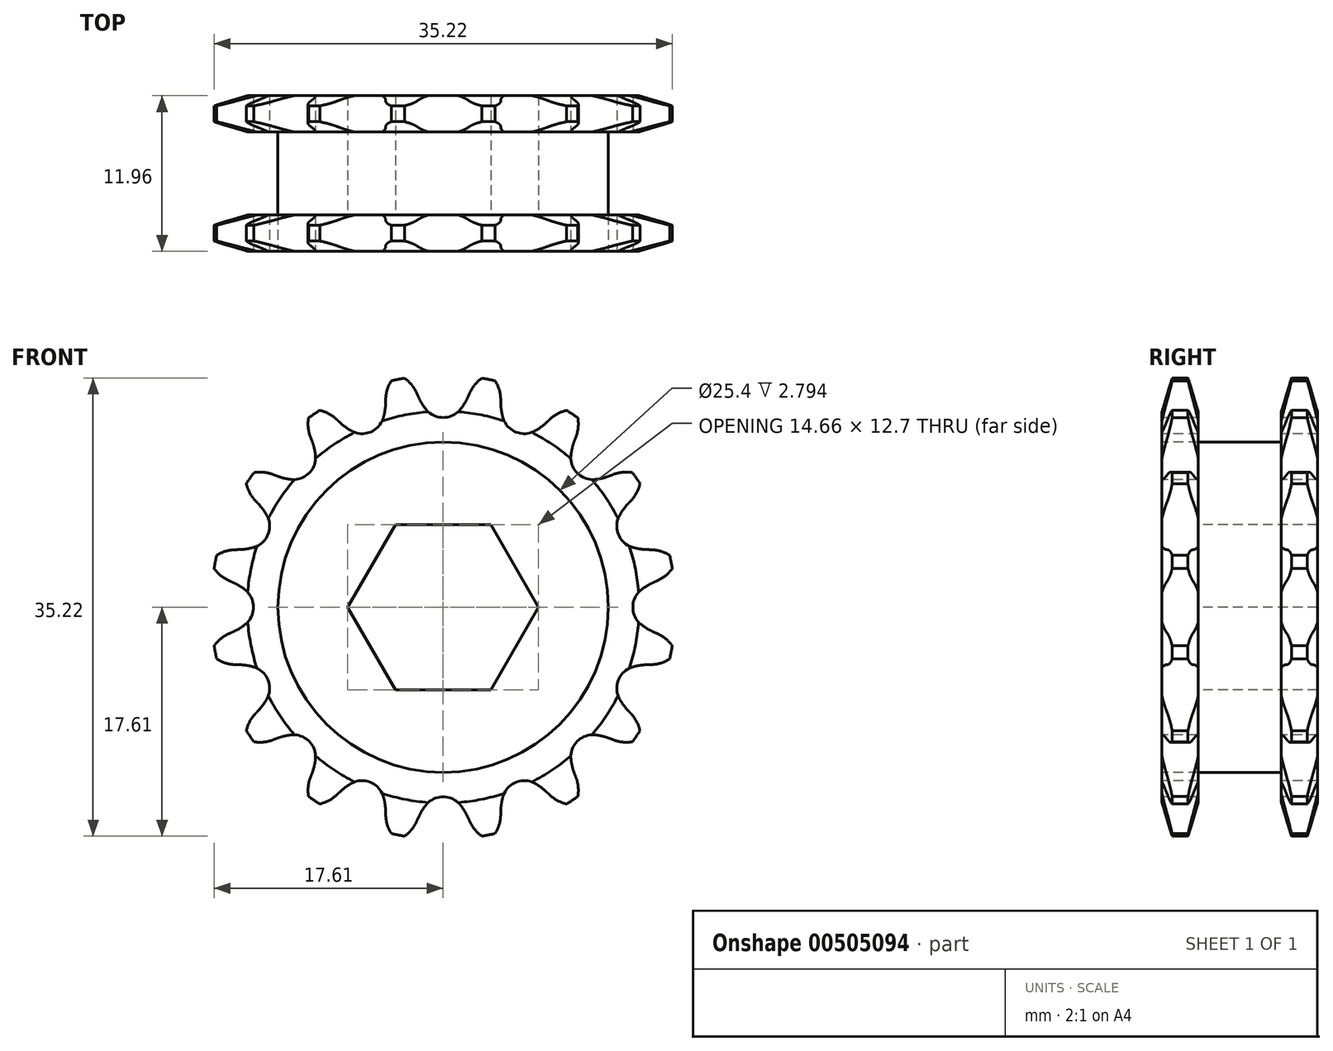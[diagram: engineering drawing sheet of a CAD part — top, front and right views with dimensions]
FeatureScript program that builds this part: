
annotation { "Feature Type Name" : "Feature", "Feature Type Description" : "" }
export const myFeature = defineFeature(function(context is Context, id is Id, definition is map)
    precondition{}
    {
        {
            var Q0;
            Q0=qCreatedBy(makeId("Right.planeOp"),FACE);
            var sketch = newSketch(context, id + "F0", { "sketchPlane" : qUnion([Q0])});
            skLineSegment(sketch, "E0", {"start": v(0, 0) * mm, "end": v(11.72, 0) * mm, "construction": true});
            skLineSegment(sketch, "E1.bottom", {"start": v(0, 3.18) * mm, "end": v(2.8, 3.18) * mm});
            skLineSegment(sketch, "E1.top", {"start": v(0, 17.86) * mm, "end": v(2.8, 17.86) * mm});
            skLineSegment(sketch, "E1.left", {"start": v(0, 3.18) * mm, "end": v(0, 17.86) * mm});
            skLineSegment(sketch, "E1.right", {"start": v(2.8, 3.18) * mm, "end": v(2.8, 17.86) * mm});
            skLineSegment(sketch, "E2.bottom", {"start": v(0, 3.18) * mm, "end": v(9.17, 3.18) * mm});
            skLineSegment(sketch, "E2.top", {"start": v(0, 12.7) * mm, "end": v(9.17, 12.7) * mm});
            skLineSegment(sketch, "E2.left", {"start": v(0, 3.18) * mm, "end": v(0, 12.7) * mm});
            skLineSegment(sketch, "E2.right", {"start": v(9.17, 3.18) * mm, "end": v(9.17, 12.7) * mm});
            skLineSegment(sketch, "E3.MirrorCS", {"start": v(0, -17.86) * mm, "end": v(2.8, -17.86) * mm});
            skLineSegment(sketch, "E4.MirrorCS", {"start": v(0, -3.18) * mm, "end": v(2.8, -3.18) * mm});
            skLineSegment(sketch, "E5.MirrorCS", {"start": v(9.17, -3.18) * mm, "end": v(9.17, -12.7) * mm});
            skLineSegment(sketch, "E6.MirrorCS", {"start": v(0, -3.18) * mm, "end": v(0, -17.86) * mm});
            skLineSegment(sketch, "E7.MirrorCS", {"start": v(2.8, -3.18) * mm, "end": v(2.8, -17.86) * mm});
            skLineSegment(sketch, "E8.MirrorCS", {"start": v(0, -3.18) * mm, "end": v(9.17, -3.18) * mm});
            skLineSegment(sketch, "E9.MirrorCS", {"start": v(0, -12.7) * mm, "end": v(9.17, -12.7) * mm});
            skLineSegment(sketch, "E10.MirrorCS", {"start": v(0, -3.18) * mm, "end": v(0, -12.7) * mm});
            skLineSegment(sketch, "E11.bottom", {"start": v(9.17, 3.18) * mm, "end": v(11.96, 3.18) * mm});
            skLineSegment(sketch, "E11.top", {"start": v(9.17, 17.86) * mm, "end": v(11.96, 17.86) * mm});
            skLineSegment(sketch, "E11.left", {"start": v(9.17, 3.18) * mm, "end": v(9.17, 17.86) * mm});
            skLineSegment(sketch, "E11.right", {"start": v(11.96, 3.18) * mm, "end": v(11.96, 17.86) * mm});
            skLineSegment(sketch, "E12.MirrorCS", {"start": v(9.17, -3.18) * mm, "end": v(9.17, -17.86) * mm});
            skLineSegment(sketch, "E13.MirrorCS", {"start": v(9.17, -17.86) * mm, "end": v(11.96, -17.86) * mm});
            skLineSegment(sketch, "E14.MirrorCS", {"start": v(11.96, -3.18) * mm, "end": v(11.96, -17.86) * mm});
            skLineSegment(sketch, "E15.MirrorCS", {"start": v(9.17, -3.18) * mm, "end": v(11.96, -3.18) * mm});
            skSolve(sketch);
        }
        {
            var Q0;
            {var subQ0=sQuery(id+"F0.wireOp",EDGE,"E1.top");Q0=makeQuery(id+"F0.imprint","IMPRINT",FACE,{"disambiguationData":[TD([[makeQuery(id+"F0.imprint","IMPRINT",EDGE,{"derivedFrom":subQ0}),-1.0]])]});}
            var Q1;
            {var subQ5=sQuery(id+"F0.wireOp",EDGE,"E2.left");Q1=makeQuery(id+"F0.imprint","IMPRINT",FACE,{"disambiguationData":[TD([[makeQuery(id+"F0.imprint","IMPRINT",EDGE,{"derivedFrom":subQ5}),-1.0]])]});}
            var Q2;
            {var subQ0=sQuery(id+"F0.wireOp",EDGE,"E2.bottom");var subQ1=sQuery(id+"F0.wireOp",EDGE,"E1.right");var subQ2=makeQuery(id+"F0.imprint","INTERSECT",VERTEX,{"derivedFrom":[subQ1,subQ0]});Q2=makeQuery(id+"F0.imprint","IMPRINT",FACE,{"disambiguationData":[TD([[makeQuery(id+"F0.imprint","IMPRINT",EDGE,{"disambiguationData":[TD([[subQ2,-1.0]])],"derivedFrom":subQ1}),-1.0]])]});}
            var Q3;
            {var subQ3=sQuery(id+"F0.wireOp",EDGE,"E11.bottom");Q3=makeQuery(id+"F0.imprint","IMPRINT",FACE,{"disambiguationData":[TD([[makeQuery(id+"F0.imprint","IMPRINT",EDGE,{"derivedFrom":subQ3}),1.0]])]});}
            var Q4;
            Q4=sQuery(id+"F0.wireOp",EDGE,"E0");
            revolve(context, id + "F1", {"entities" : qUnion([Q0, Q1, Q2, Q3]), "axis" : qUnion([Q4]), "revolveType" : RevolveType.FULL});
        }
        {
            var Q0;
            Q0=makeQuery(id+"F1.opRevolve","SWEPT_EDGE",EDGE,{"disambiguationData":[OSD([sQuery(id+"F0.wireOp",EDGE,"E1.top"),sQuery(id+"F0.wireOp",EDGE,"E1.left")])]});
            var Q1;
            Q1=makeQuery(id+"F1.opRevolve","SWEPT_EDGE",EDGE,{"disambiguationData":[OSD([sQuery(id+"F0.wireOp",EDGE,"E1.top"),sQuery(id+"F0.wireOp",EDGE,"E1.right")])]});
            chamfer(context, id + "F2", {"entities" : qUnion([Q0, Q1]), "chamferType" : ChamferType.TWO_OFFSETS, "width1" : 2.8 * mm, "oppositeDirection" : false, "width2" : 0.79 * mm, "tangentPropagation" : true});
        }
        {
            var Q0;
            Q0=makeQuery(id+"F1.opRevolve","SWEPT_EDGE",EDGE,{"disambiguationData":[OSD([sQuery(id+"F0.wireOp",EDGE,"E11.top"),sQuery(id+"F0.wireOp",EDGE,"E11.right")])]});
            var Q1;
            Q1=makeQuery(id+"F1.opRevolve","SWEPT_EDGE",EDGE,{"disambiguationData":[OSD([sQuery(id+"F0.wireOp",EDGE,"E11.top"),sQuery(id+"F0.wireOp",EDGE,"E11.left")])]});
            chamfer(context, id + "F3", {"entities" : qUnion([Q0, Q1]), "chamferType" : ChamferType.TWO_OFFSETS, "width1" : 2.8 * mm, "oppositeDirection" : true, "width2" : 0.79 * mm, "tangentPropagation" : true});
        }
        {
            var Q0;
            Q0=makeQuery(id+"F1.opRevolve","SWEPT_FACE",FACE,{"disambiguationData":[OSD([sQuery(id+"F0.wireOp",EDGE,"E1.left"),sQuery(id+"F0.wireOp",EDGE,"E2.left")])]});
            var sketch = newSketch(context, id + "F4", { "sketchPlane" : qUnion([Q0])});
            skCircle(sketch, "E16", {"center": v(0, 0) * mm, "radius": 16.28 * mm, "construction": true});
            skLineSegment(sketch, "E17", {"start": v(0, 0) * mm, "end": v(0, 16.28) * mm, "construction": true});
            skLineSegment(sketch, "E18", {"start": v(0, 16.28) * mm, "end": v(74.18, 16.28) * mm, "construction": true});
            skLineSegment(sketch, "E19", {"start": v(0, 16.28) * mm, "end": v(2.06, 17.93) * mm, "construction": true});
            skLineSegment(sketch, "E20", {"start": v(2.06, 17.93) * mm, "end": v(-1.9, 16.15) * mm, "construction": true});
            skLineSegment(sketch, "E21", {"start": v(-1.9, 16.15) * mm, "end": v(-2.05, 16.5) * mm});
            skLineSegment(sketch, "E22", {"start": v(0, 0) * mm, "end": v(-3.56, 17.92) * mm, "construction": true});
            skArc(sketch, "E23", {"start": v(-3.56, 17.92) * mm, "mid": v(-6.4, 13.4) * mm, "end": v(-2.05, 16.5) * mm, "construction": true});
            skArc(sketch, "E24", {"start": v(-2.05, 16.5) * mm, "mid": v(-2.67, 17.35) * mm, "end": v(-3.56, 17.92) * mm});
            skLineSegment(sketch, "E25", {"start": v(13.7, -18.46) * mm, "end": v(-1.9, 16.16) * mm, "construction": true});
            skArc(sketch, "E26", {"start": v(-1.9, 16.15) * mm, "mid": v(-1.64, 15.66) * mm, "end": v(-1.32, 15.21) * mm});
            skArc(sketch, "E27", {"start": v(-1.32, 15.21) * mm, "mid": v(5.76, 20.2) * mm, "end": v(-1.9, 16.15) * mm, "construction": true});
            skArc(sketch, "E28.0.MirrorCS", {"start": v(1.9, 16.15) * mm, "mid": v(1.64, 15.66) * mm, "end": v(1.32, 15.21) * mm});
            skLineSegment(sketch, "E29.0.MirrorCS", {"start": v(1.9, 16.15) * mm, "end": v(2.05, 16.5) * mm});
            skArc(sketch, "E30.0.MirrorCS", {"start": v(2.05, 16.5) * mm, "mid": v(2.67, 17.35) * mm, "end": v(3.56, 17.92) * mm});
            skArc(sketch, "E31", {"start": v(-1.32, 15.21) * mm, "mid": v(0, 14.58) * mm, "end": v(1.32, 15.21) * mm});
            skArc(sketch, "E32", {"start": v(1.32, 15.21) * mm, "mid": v(0, 17.97) * mm, "end": v(-1.32, 15.21) * mm, "construction": true});
            skArc(sketch, "E33.1.0", {"start": v(-8.2, 14.45) * mm, "mid": v(-9.1, 15.01) * mm, "end": v(-10.15, 15.19) * mm});
            skLineSegment(sketch, "E33.1.1", {"start": v(-7.93, 14.2) * mm, "end": v(-8.2, 14.45) * mm});
            skArc(sketch, "E33.1.2", {"start": v(-7.93, 14.2) * mm, "mid": v(-7.5, 13.84) * mm, "end": v(-7.04, 13.55) * mm});
            skArc(sketch, "E33.1.3", {"start": v(-7.04, 13.55) * mm, "mid": v(-5.58, 13.47) * mm, "end": v(-4.6, 14.56) * mm});
            skArc(sketch, "E33.1.4", {"start": v(-4.43, 15.64) * mm, "mid": v(-4.48, 15.1) * mm, "end": v(-4.6, 14.56) * mm});
            skLineSegment(sketch, "E33.1.5", {"start": v(-4.43, 15.64) * mm, "end": v(-4.42, 16.02) * mm});
            skArc(sketch, "E33.1.6", {"start": v(-4.42, 16.02) * mm, "mid": v(-4.18, 17.05) * mm, "end": v(-3.56, 17.92) * mm});
            skArc(sketch, "E33.2.0", {"start": v(-13.11, 10.21) * mm, "mid": v(-14.16, 10.39) * mm, "end": v(-15.19, 10.15) * mm});
            skLineSegment(sketch, "E33.2.1", {"start": v(-12.76, 10.08) * mm, "end": v(-13.11, 10.21) * mm});
            skArc(sketch, "E33.2.2", {"start": v(-12.76, 10.08) * mm, "mid": v(-12.23, 9.91) * mm, "end": v(-11.7, 9.82) * mm});
            skArc(sketch, "E33.2.3", {"start": v(-11.7, 9.82) * mm, "mid": v(-10.3, 10.3) * mm, "end": v(-9.82, 11.7) * mm});
            skArc(sketch, "E33.2.4", {"start": v(-10.08, 12.76) * mm, "mid": v(-9.91, 12.23) * mm, "end": v(-9.82, 11.7) * mm});
            skLineSegment(sketch, "E33.2.5", {"start": v(-10.08, 12.76) * mm, "end": v(-10.21, 13.11) * mm});
            skArc(sketch, "E33.2.6", {"start": v(-10.21, 13.11) * mm, "mid": v(-10.39, 14.16) * mm, "end": v(-10.15, 15.19) * mm});
            skArc(sketch, "E33.3.0", {"start": v(-16.02, 4.42) * mm, "mid": v(-17.05, 4.18) * mm, "end": v(-17.92, 3.56) * mm});
            skLineSegment(sketch, "E33.3.1", {"start": v(-15.64, 4.43) * mm, "end": v(-16.02, 4.42) * mm});
            skArc(sketch, "E33.3.2", {"start": v(-15.64, 4.43) * mm, "mid": v(-15.1, 4.48) * mm, "end": v(-14.56, 4.6) * mm});
            skArc(sketch, "E33.3.3", {"start": v(-14.56, 4.6) * mm, "mid": v(-13.47, 5.58) * mm, "end": v(-13.55, 7.04) * mm});
            skArc(sketch, "E33.3.4", {"start": v(-14.2, 7.93) * mm, "mid": v(-13.84, 7.5) * mm, "end": v(-13.55, 7.04) * mm});
            skLineSegment(sketch, "E33.3.5", {"start": v(-14.2, 7.93) * mm, "end": v(-14.45, 8.2) * mm});
            skArc(sketch, "E33.3.6", {"start": v(-14.45, 8.2) * mm, "mid": v(-15.01, 9.1) * mm, "end": v(-15.19, 10.15) * mm});
            skArc(sketch, "E33.4.0", {"start": v(-16.5, -2.05) * mm, "mid": v(-17.35, -2.67) * mm, "end": v(-17.92, -3.56) * mm});
            skLineSegment(sketch, "E33.4.1", {"start": v(-16.15, -1.9) * mm, "end": v(-16.5, -2.05) * mm});
            skArc(sketch, "E33.4.2", {"start": v(-16.15, -1.9) * mm, "mid": v(-15.66, -1.64) * mm, "end": v(-15.21, -1.32) * mm});
            skArc(sketch, "E33.4.3", {"start": v(-15.21, -1.32) * mm, "mid": v(-14.58, 0) * mm, "end": v(-15.21, 1.32) * mm});
            skArc(sketch, "E33.4.4", {"start": v(-16.15, 1.9) * mm, "mid": v(-15.66, 1.64) * mm, "end": v(-15.21, 1.32) * mm});
            skLineSegment(sketch, "E33.4.5", {"start": v(-16.15, 1.9) * mm, "end": v(-16.5, 2.05) * mm});
            skArc(sketch, "E33.4.6", {"start": v(-16.5, 2.05) * mm, "mid": v(-17.35, 2.67) * mm, "end": v(-17.92, 3.56) * mm});
            skArc(sketch, "E33.5.0", {"start": v(-14.45, -8.2) * mm, "mid": v(-15.01, -9.1) * mm, "end": v(-15.19, -10.15) * mm});
            skLineSegment(sketch, "E33.5.1", {"start": v(-14.2, -7.93) * mm, "end": v(-14.45, -8.2) * mm});
            skArc(sketch, "E33.5.2", {"start": v(-14.2, -7.93) * mm, "mid": v(-13.84, -7.5) * mm, "end": v(-13.55, -7.04) * mm});
            skArc(sketch, "E33.5.3", {"start": v(-13.55, -7.04) * mm, "mid": v(-13.47, -5.58) * mm, "end": v(-14.56, -4.6) * mm});
            skArc(sketch, "E33.5.4", {"start": v(-15.64, -4.43) * mm, "mid": v(-15.1, -4.48) * mm, "end": v(-14.56, -4.6) * mm});
            skLineSegment(sketch, "E33.5.5", {"start": v(-15.64, -4.43) * mm, "end": v(-16.02, -4.42) * mm});
            skArc(sketch, "E33.5.6", {"start": v(-16.02, -4.42) * mm, "mid": v(-17.05, -4.18) * mm, "end": v(-17.92, -3.56) * mm});
            skArc(sketch, "E33.6.0", {"start": v(-10.21, -13.11) * mm, "mid": v(-10.39, -14.16) * mm, "end": v(-10.15, -15.19) * mm});
            skLineSegment(sketch, "E33.6.1", {"start": v(-10.08, -12.76) * mm, "end": v(-10.21, -13.11) * mm});
            skArc(sketch, "E33.6.2", {"start": v(-10.08, -12.76) * mm, "mid": v(-9.91, -12.23) * mm, "end": v(-9.82, -11.7) * mm});
            skArc(sketch, "E33.6.3", {"start": v(-9.82, -11.7) * mm, "mid": v(-10.3, -10.3) * mm, "end": v(-11.7, -9.82) * mm});
            skArc(sketch, "E33.6.4", {"start": v(-12.76, -10.08) * mm, "mid": v(-12.23, -9.91) * mm, "end": v(-11.7, -9.82) * mm});
            skLineSegment(sketch, "E33.6.5", {"start": v(-12.76, -10.08) * mm, "end": v(-13.11, -10.21) * mm});
            skArc(sketch, "E33.6.6", {"start": v(-13.11, -10.21) * mm, "mid": v(-14.16, -10.39) * mm, "end": v(-15.19, -10.15) * mm});
            skArc(sketch, "E33.7.0", {"start": v(-4.42, -16.02) * mm, "mid": v(-4.18, -17.05) * mm, "end": v(-3.56, -17.92) * mm});
            skLineSegment(sketch, "E33.7.1", {"start": v(-4.43, -15.64) * mm, "end": v(-4.42, -16.02) * mm});
            skArc(sketch, "E33.7.2", {"start": v(-4.43, -15.64) * mm, "mid": v(-4.48, -15.1) * mm, "end": v(-4.6, -14.56) * mm});
            skArc(sketch, "E33.7.3", {"start": v(-4.6, -14.56) * mm, "mid": v(-5.58, -13.47) * mm, "end": v(-7.04, -13.55) * mm});
            skArc(sketch, "E33.7.4", {"start": v(-7.93, -14.2) * mm, "mid": v(-7.5, -13.84) * mm, "end": v(-7.04, -13.55) * mm});
            skLineSegment(sketch, "E33.7.5", {"start": v(-7.93, -14.2) * mm, "end": v(-8.2, -14.45) * mm});
            skArc(sketch, "E33.7.6", {"start": v(-8.2, -14.45) * mm, "mid": v(-9.1, -15.01) * mm, "end": v(-10.15, -15.19) * mm});
            skArc(sketch, "E33.8.0", {"start": v(2.05, -16.5) * mm, "mid": v(2.67, -17.35) * mm, "end": v(3.56, -17.92) * mm});
            skLineSegment(sketch, "E33.8.1", {"start": v(1.9, -16.15) * mm, "end": v(2.05, -16.5) * mm});
            skArc(sketch, "E33.8.2", {"start": v(1.9, -16.15) * mm, "mid": v(1.64, -15.66) * mm, "end": v(1.32, -15.21) * mm});
            skArc(sketch, "E33.8.3", {"start": v(1.32, -15.21) * mm, "mid": v(0, -14.58) * mm, "end": v(-1.32, -15.21) * mm});
            skArc(sketch, "E33.8.4", {"start": v(-1.9, -16.15) * mm, "mid": v(-1.64, -15.66) * mm, "end": v(-1.32, -15.21) * mm});
            skLineSegment(sketch, "E33.8.5", {"start": v(-1.9, -16.15) * mm, "end": v(-2.05, -16.5) * mm});
            skArc(sketch, "E33.8.6", {"start": v(-2.05, -16.5) * mm, "mid": v(-2.67, -17.35) * mm, "end": v(-3.56, -17.92) * mm});
            skArc(sketch, "E33.9.0", {"start": v(8.2, -14.45) * mm, "mid": v(9.1, -15.01) * mm, "end": v(10.15, -15.19) * mm});
            skLineSegment(sketch, "E33.9.1", {"start": v(7.93, -14.2) * mm, "end": v(8.2, -14.45) * mm});
            skArc(sketch, "E33.9.2", {"start": v(7.93, -14.2) * mm, "mid": v(7.5, -13.84) * mm, "end": v(7.04, -13.55) * mm});
            skArc(sketch, "E33.9.3", {"start": v(7.04, -13.55) * mm, "mid": v(5.58, -13.47) * mm, "end": v(4.6, -14.56) * mm});
            skArc(sketch, "E33.9.4", {"start": v(4.43, -15.64) * mm, "mid": v(4.48, -15.1) * mm, "end": v(4.6, -14.56) * mm});
            skLineSegment(sketch, "E33.9.5", {"start": v(4.43, -15.64) * mm, "end": v(4.42, -16.02) * mm});
            skArc(sketch, "E33.9.6", {"start": v(4.42, -16.02) * mm, "mid": v(4.18, -17.05) * mm, "end": v(3.56, -17.92) * mm});
            skArc(sketch, "E33.10.0", {"start": v(13.11, -10.21) * mm, "mid": v(14.16, -10.39) * mm, "end": v(15.19, -10.15) * mm});
            skLineSegment(sketch, "E33.10.1", {"start": v(12.76, -10.08) * mm, "end": v(13.11, -10.21) * mm});
            skArc(sketch, "E33.10.2", {"start": v(12.76, -10.08) * mm, "mid": v(12.23, -9.91) * mm, "end": v(11.7, -9.82) * mm});
            skArc(sketch, "E33.10.3", {"start": v(11.7, -9.82) * mm, "mid": v(10.3, -10.3) * mm, "end": v(9.82, -11.7) * mm});
            skArc(sketch, "E33.10.4", {"start": v(10.08, -12.76) * mm, "mid": v(9.91, -12.23) * mm, "end": v(9.82, -11.7) * mm});
            skLineSegment(sketch, "E33.10.5", {"start": v(10.08, -12.76) * mm, "end": v(10.21, -13.11) * mm});
            skArc(sketch, "E33.10.6", {"start": v(10.21, -13.11) * mm, "mid": v(10.39, -14.16) * mm, "end": v(10.15, -15.19) * mm});
            skArc(sketch, "E33.11.0", {"start": v(16.02, -4.42) * mm, "mid": v(17.05, -4.18) * mm, "end": v(17.92, -3.56) * mm});
            skLineSegment(sketch, "E33.11.1", {"start": v(15.64, -4.43) * mm, "end": v(16.02, -4.42) * mm});
            skArc(sketch, "E33.11.2", {"start": v(15.64, -4.43) * mm, "mid": v(15.1, -4.48) * mm, "end": v(14.56, -4.6) * mm});
            skArc(sketch, "E33.11.3", {"start": v(14.56, -4.6) * mm, "mid": v(13.47, -5.58) * mm, "end": v(13.55, -7.04) * mm});
            skArc(sketch, "E33.11.4", {"start": v(14.2, -7.93) * mm, "mid": v(13.84, -7.5) * mm, "end": v(13.55, -7.04) * mm});
            skLineSegment(sketch, "E33.11.5", {"start": v(14.2, -7.93) * mm, "end": v(14.45, -8.2) * mm});
            skArc(sketch, "E33.11.6", {"start": v(14.45, -8.2) * mm, "mid": v(15.01, -9.1) * mm, "end": v(15.19, -10.15) * mm});
            skArc(sketch, "E33.12.0", {"start": v(16.5, 2.05) * mm, "mid": v(17.35, 2.67) * mm, "end": v(17.92, 3.56) * mm});
            skLineSegment(sketch, "E33.12.1", {"start": v(16.15, 1.9) * mm, "end": v(16.5, 2.05) * mm});
            skArc(sketch, "E33.12.2", {"start": v(16.15, 1.9) * mm, "mid": v(15.66, 1.64) * mm, "end": v(15.21, 1.32) * mm});
            skArc(sketch, "E33.12.3", {"start": v(15.21, 1.32) * mm, "mid": v(14.58, 0) * mm, "end": v(15.21, -1.32) * mm});
            skArc(sketch, "E33.12.4", {"start": v(16.15, -1.9) * mm, "mid": v(15.66, -1.64) * mm, "end": v(15.21, -1.32) * mm});
            skLineSegment(sketch, "E33.12.5", {"start": v(16.15, -1.9) * mm, "end": v(16.5, -2.05) * mm});
            skArc(sketch, "E33.12.6", {"start": v(16.5, -2.05) * mm, "mid": v(17.35, -2.67) * mm, "end": v(17.92, -3.56) * mm});
            skArc(sketch, "E33.13.0", {"start": v(14.45, 8.2) * mm, "mid": v(15.01, 9.1) * mm, "end": v(15.19, 10.15) * mm});
            skLineSegment(sketch, "E33.13.1", {"start": v(14.2, 7.93) * mm, "end": v(14.45, 8.2) * mm});
            skArc(sketch, "E33.13.2", {"start": v(14.2, 7.93) * mm, "mid": v(13.84, 7.5) * mm, "end": v(13.55, 7.04) * mm});
            skArc(sketch, "E33.13.3", {"start": v(13.55, 7.04) * mm, "mid": v(13.47, 5.58) * mm, "end": v(14.56, 4.6) * mm});
            skArc(sketch, "E33.13.4", {"start": v(15.64, 4.43) * mm, "mid": v(15.1, 4.48) * mm, "end": v(14.56, 4.6) * mm});
            skLineSegment(sketch, "E33.13.5", {"start": v(15.64, 4.43) * mm, "end": v(16.02, 4.42) * mm});
            skArc(sketch, "E33.13.6", {"start": v(16.02, 4.42) * mm, "mid": v(17.05, 4.18) * mm, "end": v(17.92, 3.56) * mm});
            skArc(sketch, "E33.14.0", {"start": v(10.21, 13.11) * mm, "mid": v(10.39, 14.16) * mm, "end": v(10.15, 15.19) * mm});
            skLineSegment(sketch, "E33.14.1", {"start": v(10.08, 12.76) * mm, "end": v(10.21, 13.11) * mm});
            skArc(sketch, "E33.14.2", {"start": v(10.08, 12.76) * mm, "mid": v(9.91, 12.23) * mm, "end": v(9.82, 11.7) * mm});
            skArc(sketch, "E33.14.3", {"start": v(9.82, 11.7) * mm, "mid": v(10.3, 10.3) * mm, "end": v(11.7, 9.82) * mm});
            skArc(sketch, "E33.14.4", {"start": v(12.76, 10.08) * mm, "mid": v(12.23, 9.91) * mm, "end": v(11.7, 9.82) * mm});
            skLineSegment(sketch, "E33.14.5", {"start": v(12.76, 10.08) * mm, "end": v(13.11, 10.21) * mm});
            skArc(sketch, "E33.14.6", {"start": v(13.11, 10.21) * mm, "mid": v(14.16, 10.39) * mm, "end": v(15.19, 10.15) * mm});
            skArc(sketch, "E33.15.0", {"start": v(4.42, 16.02) * mm, "mid": v(4.18, 17.05) * mm, "end": v(3.56, 17.92) * mm});
            skLineSegment(sketch, "E33.15.1", {"start": v(4.43, 15.64) * mm, "end": v(4.42, 16.02) * mm});
            skArc(sketch, "E33.15.2", {"start": v(4.43, 15.64) * mm, "mid": v(4.48, 15.1) * mm, "end": v(4.6, 14.56) * mm});
            skArc(sketch, "E33.15.3", {"start": v(4.6, 14.56) * mm, "mid": v(5.58, 13.47) * mm, "end": v(7.04, 13.55) * mm});
            skArc(sketch, "E33.15.4", {"start": v(7.93, 14.2) * mm, "mid": v(7.5, 13.84) * mm, "end": v(7.04, 13.55) * mm});
            skLineSegment(sketch, "E33.15.5", {"start": v(7.93, 14.2) * mm, "end": v(8.2, 14.45) * mm});
            skArc(sketch, "E33.15.6", {"start": v(8.2, 14.45) * mm, "mid": v(9.1, 15.01) * mm, "end": v(10.15, 15.19) * mm});
            skSolve(sketch);
        }
        {
            var Q0;
            Q0=qSketchRegion(id+"F4",true);
            extrude(context, id + "F5", {"entities" : qUnion([Q0]), "operationType" : NewBodyOperationType.INTERSECT, "endBound" : BoundingType.THROUGH_ALL, "oppositeDirection" : true, "depth" : 25.4 * mm});
        }
        {
            var Q0;
            Q0=makeQuery(id+"F1.opRevolve","SWEPT_FACE",FACE,{"disambiguationData":[OSD([sQuery(id+"F0.wireOp",EDGE,"E1.left"),sQuery(id+"F0.wireOp",EDGE,"E2.left")])]});
            var sketch = newSketch(context, id + "F6", { "sketchPlane" : qUnion([Q0])});
            skCircle(sketch, "E34.cCircle", {"center": v(0, 0) * mm, "radius": 6.35 * mm, "construction": true});
            skLineSegment(sketch, "E34.0", {"start": v(-3.67, 6.35) * mm, "end": v(3.67, 6.35) * mm});
            skLineSegment(sketch, "E34.1", {"start": v(3.67, 6.35) * mm, "end": v(7.33, 0) * mm});
            skLineSegment(sketch, "E34.2", {"start": v(7.33, 0) * mm, "end": v(3.67, -6.35) * mm});
            skLineSegment(sketch, "E34.3", {"start": v(3.67, -6.35) * mm, "end": v(-3.67, -6.35) * mm});
            skLineSegment(sketch, "E34.4", {"start": v(-3.67, -6.35) * mm, "end": v(-7.33, 0) * mm});
            skLineSegment(sketch, "E34.5", {"start": v(-7.33, 0) * mm, "end": v(-3.67, 6.35) * mm});
            skPoint(sketch, "E34.0.midPoint", {"position": v(0, 6.35) * mm});
            skSolve(sketch);
        }
        {
            var Q0;
            Q0=qSketchRegion(id+"F6",true);
            extrude(context, id + "F7", {"entities" : qUnion([Q0]), "operationType" : NewBodyOperationType.REMOVE, "endBound" : BoundingType.THROUGH_ALL, "oppositeDirection" : true, "depth" : 25.4 * mm});
        }
    });
